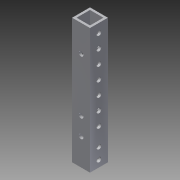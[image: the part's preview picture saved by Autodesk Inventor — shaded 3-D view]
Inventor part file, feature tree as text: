
AUTODESK INVENTOR PART (.ipt)
format: ipt  version: 2014 SP1 (Build 180222100, 222)  size: 145,920 bytes
history: native  units: in
note: dims shown in document units (in); Inventor stores cm internally (conversion verified against a paired STEP export)
features: extrude x4, sketch x4, reference x2
ambient origin geometry x8: Origin, YZ Plane, XZ Plane, XY Plane, X Axis, Y Axis, Z Axis, Center Point
bodies: Solid1 (feature_tree)
feature tree (10):
  extrude  "Extrusion1"  Depth=1.0in
  extrude  "Extrusion2"  Depth=7.0in TaperAngle=0.0deg
  extrude  "Extrusion3"  Depth=1.0in
  extrude  "Extrusion4"  Depth=1.0in
  sketch  "Sketch1"  dims[d0=1.0in d1=1.0in]
  sketch  "Sketch2"  dims[d2=0.125in d3=7.0in d4=0.0in]
  reference  "Reference1"
  reference  "Reference2"
  sketch  "Sketch3"  dims[d7=1.0in d8=0.0in d17=0.26in]
  sketch  "Sketch4"  dims[d18=0.26in d19=4.25in d20=0.26in d21=0.5in d22=0.5in d23=0.26in d25=1.0in d26=2.3622in d28=0.75in d29=0.3937in d31=1.0in d33=1.0in d34=0.0in d35=1.5in d36=0.26in d37=1.9685in d39=1.0in d40=0.3937in d42=1.0in d44=1.0in d45=0.0in]
